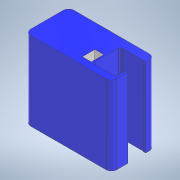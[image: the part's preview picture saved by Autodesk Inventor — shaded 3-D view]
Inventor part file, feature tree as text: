
AUTODESK INVENTOR PART (.ipt)
format: ipt  version: 2022 (Build 260153000, 153)  size: 168,448 bytes
history: native  units: mm
features: other x7, reference x3, direct_edit x1, extrude x1, sketch x1, move_body x1
ambient origin geometry x8: Origin, YZ Plane, XZ Plane, XY Plane, X Axis, Y Axis, Z Axis, Center Point
bodies: Solid1 (feature_tree)
feature tree (14):
  other  "Z Belt Housing.ipt"
  direct_edit  "Direct Edit1"
  extrude  "Extrusion1"  Depth=10.0mm TaperAngle=0.0deg
  other  "Solid1::Z Belt Housing.ipt"
  other  "TaggingFeature1"
  sketch  "Sketch1"  dims[d0=10.0mm d1=0.0mm d2=0.0mm d3=10.0mm d4=2.0mm d5=5.0mm d6=0.0mm d7=0.0mm]
  reference  "Reference1"
  reference  "Reference2"
  reference  "Reference3"
  move_body  "Move1"
  parser-record x1  (decoder bookkeeping rows leaked as tree rows — omitted from the tree; the rows remain in map.json)
  other  "Bibble0.iam"
  other  "Alternate Z Drive Assembly:1"
  other  "GT2 Pulley 16T:1"
note: 1 file-system path scrubbed to <path> (originals preserved in map.json)
